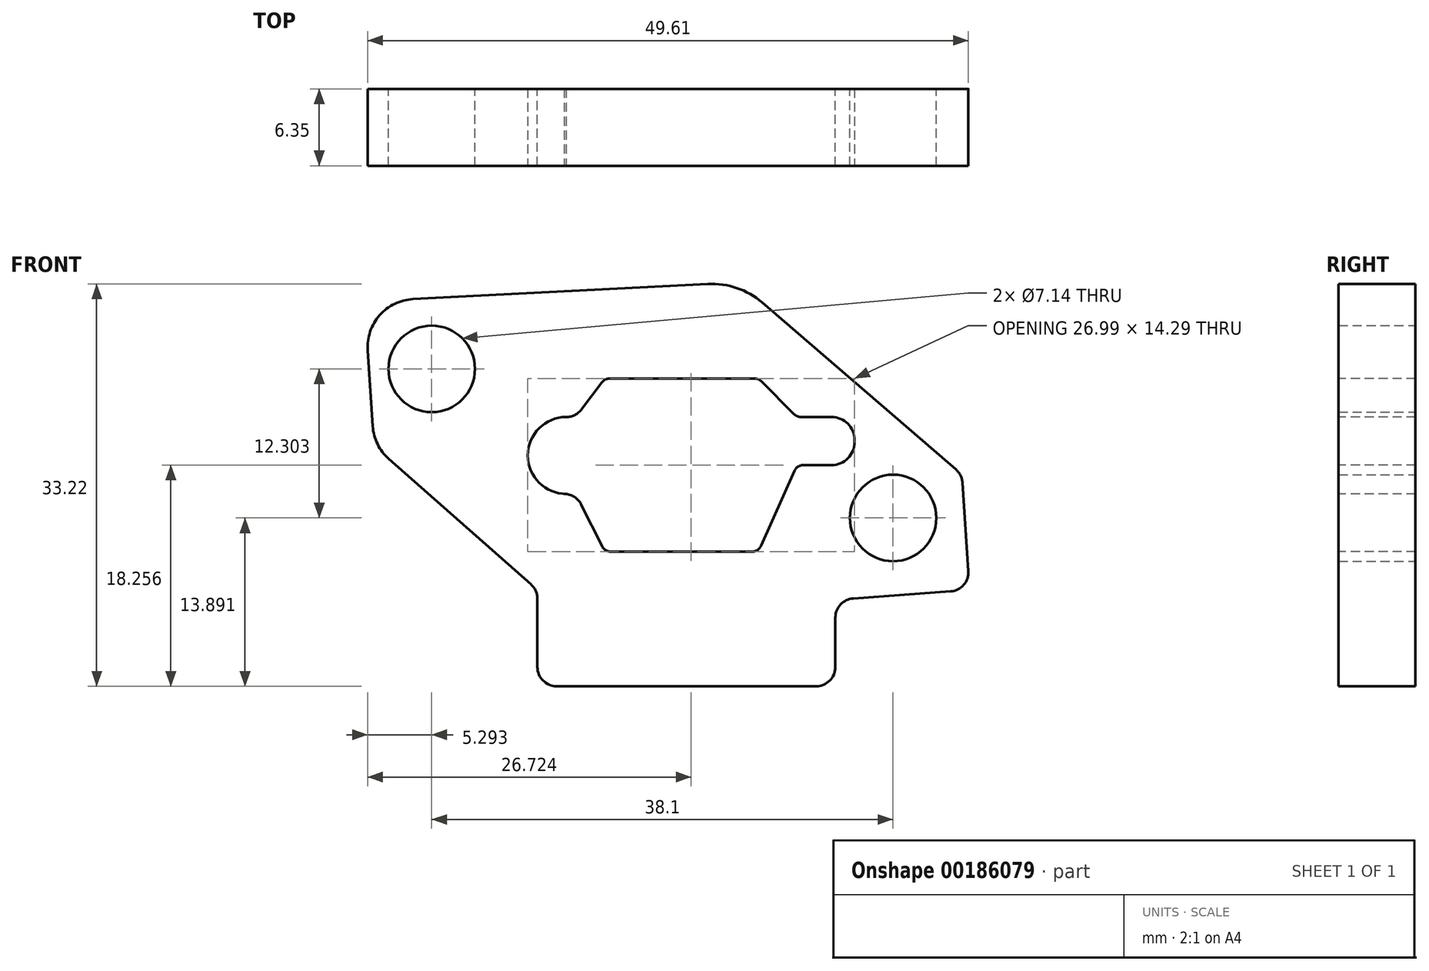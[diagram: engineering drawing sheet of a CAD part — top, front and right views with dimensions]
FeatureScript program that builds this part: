
annotation { "Feature Type Name" : "Feature", "Feature Type Description" : "" }
export const myFeature = defineFeature(function(context is Context, id is Id, definition is map)
    precondition{}
    {
        {
            var Q0;
            Q0=qCreatedBy(makeId("Front.planeOp"),FACE);
            var sketch = newSketch(context, id + "F0", { "sketchPlane" : qUnion([Q0])});
            skLineSegment(sketch, "E0", {"start": v(-1.59, 0) * mm, "end": v(-23.02, 0) * mm});
            skLineSegment(sketch, "E1", {"start": v(-24.6, 1.59) * mm, "end": v(-24.6, 7.22) * mm});
            skLineSegment(sketch, "E2", {"start": v(-25.14, 8.41) * mm, "end": v(-36.87, 18.76) * mm});
            skLineSegment(sketch, "E3", {"start": v(-38.2, 21.47) * mm, "end": v(-38.63, 27.73) * mm});
            skLineSegment(sketch, "E4", {"start": v(-34.87, 31.96) * mm, "end": v(-10.52, 33.2) * mm});
            skLineSegment(sketch, "E5", {"start": v(-6.05, 31.68) * mm, "end": v(9.95, 17.9) * mm});
            skLineSegment(sketch, "E6", {"start": v(10.5, 16.8) * mm, "end": v(10.98, 9.51) * mm});
            skLineSegment(sketch, "E7", {"start": v(9.5, 7.82) * mm, "end": v(1.47, 7.25) * mm});
            skLineSegment(sketch, "E8", {"start": v(0, 5.67) * mm, "end": v(0, 1.59) * mm});
            skPoint(sketch, "E9.visualSharp", {"position": v(-38.9, 31.75) * mm});
            skArc(sketch, "E9.filletArc", {"start": v(-34.87, 31.96) * mm, "mid": v(-37.63, 30.63) * mm, "end": v(-38.63, 27.73) * mm});
            skPoint(sketch, "E10.visualSharp", {"position": v(-38.1, 19.84) * mm});
            skArc(sketch, "E10.filletArc", {"start": v(-38.2, 21.47) * mm, "mid": v(-37.8, 19.99) * mm, "end": v(-36.87, 18.76) * mm});
            skPoint(sketch, "E11.visualSharp", {"position": v(-7.98, 33.34) * mm});
            skArc(sketch, "E11.filletArc", {"start": v(-6.05, 31.68) * mm, "mid": v(-8.14, 32.87) * mm, "end": v(-10.52, 33.2) * mm});
            skPoint(sketch, "E12.visualSharp", {"position": v(11.08, 7.94) * mm});
            skArc(sketch, "E12.filletArc", {"start": v(9.5, 7.82) * mm, "mid": v(10.6, 8.37) * mm, "end": v(10.98, 9.51) * mm});
            skPoint(sketch, "E13.visualSharp", {"position": v(10.45, 17.46) * mm});
            skArc(sketch, "E13.filletArc", {"start": v(10.5, 16.8) * mm, "mid": v(10.33, 17.4) * mm, "end": v(9.95, 17.9) * mm});
            skPoint(sketch, "E14.visualSharp", {"position": v(0, 7.14) * mm});
            skArc(sketch, "E14.filletArc", {"start": v(1.47, 7.25) * mm, "mid": v(0.43, 6.75) * mm, "end": v(0, 5.67) * mm});
            skPoint(sketch, "E15.visualSharp", {"position": v(0, 0) * mm});
            skArc(sketch, "E15.filletArc", {"start": v(-1.59, 0) * mm, "mid": v(-0.46, 0.46) * mm, "end": v(0, 1.59) * mm});
            skPoint(sketch, "E16.visualSharp", {"position": v(-24.6, 0) * mm});
            skArc(sketch, "E16.filletArc", {"start": v(-24.6, 1.59) * mm, "mid": v(-24.14, 0.46) * mm, "end": v(-23.02, 0) * mm});
            skPoint(sketch, "E17.visualSharp", {"position": v(-24.6, 7.94) * mm});
            skArc(sketch, "E17.filletArc", {"start": v(-24.6, 7.22) * mm, "mid": v(-24.75, 7.87) * mm, "end": v(-25.14, 8.41) * mm});
            skCircle(sketch, "E18", {"center": v(-33.34, 26.2) * mm, "radius": 3.57 * mm});
            skCircle(sketch, "E19", {"center": v(4.76, 13.9) * mm, "radius": 3.57 * mm});
            skSolve(sketch);
        }
        {
            var Q0;
            Q0=makeQuery(id+"F0.imprint","IMPRINT",FACE,{"disambiguationData":[TD([[makeQuery(id+"F0.imprint","IMPRINT",EDGE,{"derivedFrom":sQuery(id+"F0.wireOp",EDGE,"E0")}),-1.0]])]});
            extrude(context, id + "F1", {"entities" : qUnion([Q0]), "depth" : 6.35 * mm});
        }
        {
            var Q0;
            Q0=makeQuery(id+"F1.opExtrude","CAP_FACE",FACE,{"disambiguationData":[OSD([sQuery(id+"F0.wireOp",EDGE,"E0"),sQuery(id+"F0.wireOp",EDGE,"E1"),sQuery(id+"F0.wireOp",EDGE,"E2"),sQuery(id+"F0.wireOp",EDGE,"E3"),sQuery(id+"F0.wireOp",EDGE,"E4"),sQuery(id+"F0.wireOp",EDGE,"E5"),sQuery(id+"F0.wireOp",EDGE,"E6"),sQuery(id+"F0.wireOp",EDGE,"E7"),sQuery(id+"F0.wireOp",EDGE,"E8"),sQuery(id+"F0.wireOp",EDGE,"E9.filletArc"),sQuery(id+"F0.wireOp",EDGE,"E10.filletArc"),sQuery(id+"F0.wireOp",EDGE,"E11.filletArc"),sQuery(id+"F0.wireOp",EDGE,"E12.filletArc"),sQuery(id+"F0.wireOp",EDGE,"E13.filletArc"),sQuery(id+"F0.wireOp",EDGE,"E14.filletArc"),sQuery(id+"F0.wireOp",EDGE,"E15.filletArc"),sQuery(id+"F0.wireOp",EDGE,"E16.filletArc"),sQuery(id+"F0.wireOp",EDGE,"E17.filletArc"),sQuery(id+"F0.wireOp",EDGE,"E18"),sQuery(id+"F0.wireOp",EDGE,"E19")])],"isStart":false});
            var sketch = newSketch(context, id + "F2", { "sketchPlane" : qUnion([Q0])});
            skLineSegment(sketch, "E20", {"start": v(-18.56, 11.11) * mm, "end": v(-6.87, 11.11) * mm});
            skLineSegment(sketch, "E21", {"start": v(-6.14, 11.58) * mm, "end": v(-3.38, 17.78) * mm});
            skLineSegment(sketch, "E22", {"start": v(-2.66, 18.26) * mm, "end": v(-0.32, 18.26) * mm});
            skLineSegment(sketch, "E23", {"start": v(1.59, 20.16) * mm, "end": v(1.59, 20.32) * mm});
            skLineSegment(sketch, "E24", {"start": v(-0.32, 22.23) * mm, "end": v(-2.85, 22.23) * mm});
            skLineSegment(sketch, "E25", {"start": v(-3.4, 22.46) * mm, "end": v(-6.12, 25.17) * mm});
            skLineSegment(sketch, "E26", {"start": v(-6.68, 25.4) * mm, "end": v(-18.65, 25.4) * mm});
            skLineSegment(sketch, "E27", {"start": v(-19.29, 25.08) * mm, "end": v(-20.96, 22.86) * mm});
            skLineSegment(sketch, "E28", {"start": v(-22.23, 22.23) * mm, "end": v(-22.23, 22.23) * mm});
            skLineSegment(sketch, "E29", {"start": v(-25.4, 19.05) * mm, "end": v(-25.4, 19.05) * mm});
            skLineSegment(sketch, "E30", {"start": v(-22.41, 15.88) * mm, "end": v(-22.23, 15.88) * mm});
            skLineSegment(sketch, "E31", {"start": v(-21, 15) * mm, "end": v(-19.27, 11.55) * mm});
            skPoint(sketch, "E32.visualSharp", {"position": v(-25.4, 22.23) * mm});
            skArc(sketch, "E32.filletArc", {"start": v(-22.23, 22.23) * mm, "mid": v(-24.47, 21.3) * mm, "end": v(-25.4, 19.05) * mm});
            skPoint(sketch, "E33.visualSharp", {"position": v(-25.4, 15.88) * mm});
            skArc(sketch, "E33.filletArc", {"start": v(-25.4, 19.05) * mm, "mid": v(-24.47, 16.8) * mm, "end": v(-22.23, 15.88) * mm});
            skPoint(sketch, "E34.visualSharp", {"position": v(-21.43, 22.23) * mm});
            skArc(sketch, "E34.filletArc", {"start": v(-22.23, 22.23) * mm, "mid": v(-21.52, 22.4) * mm, "end": v(-20.96, 22.86) * mm});
            skPoint(sketch, "E35.visualSharp", {"position": v(-19.05, 25.4) * mm});
            skArc(sketch, "E35.filletArc", {"start": v(-18.65, 25.4) * mm, "mid": v(-19, 25.32) * mm, "end": v(-19.29, 25.08) * mm});
            skPoint(sketch, "E36.visualSharp", {"position": v(-6.35, 25.4) * mm});
            skArc(sketch, "E36.filletArc", {"start": v(-6.12, 25.17) * mm, "mid": v(-6.38, 25.34) * mm, "end": v(-6.68, 25.4) * mm});
            skPoint(sketch, "E37.visualSharp", {"position": v(-3.18, 22.22) * mm});
            skArc(sketch, "E37.filletArc", {"start": v(-3.4, 22.46) * mm, "mid": v(-3.15, 22.29) * mm, "end": v(-2.85, 22.23) * mm});
            skPoint(sketch, "E38.visualSharp", {"position": v(1.59, 22.23) * mm});
            skArc(sketch, "E38.filletArc", {"start": v(1.59, 20.32) * mm, "mid": v(1.03, 21.67) * mm, "end": v(-0.32, 22.23) * mm});
            skPoint(sketch, "E39.visualSharp", {"position": v(1.59, 18.26) * mm});
            skArc(sketch, "E39.filletArc", {"start": v(-0.32, 18.26) * mm, "mid": v(1.03, 18.81) * mm, "end": v(1.59, 20.16) * mm});
            skPoint(sketch, "E40.visualSharp", {"position": v(-6.35, 11.11) * mm});
            skArc(sketch, "E40.filletArc", {"start": v(-6.87, 11.11) * mm, "mid": v(-6.43, 11.24) * mm, "end": v(-6.14, 11.58) * mm});
            skPoint(sketch, "E41.visualSharp", {"position": v(-3.18, 18.26) * mm});
            skArc(sketch, "E41.filletArc", {"start": v(-2.66, 18.26) * mm, "mid": v(-3.1, 18.13) * mm, "end": v(-3.38, 17.78) * mm});
            skPoint(sketch, "E42.visualSharp", {"position": v(-19.05, 11.11) * mm});
            skArc(sketch, "E42.filletArc", {"start": v(-19.27, 11.55) * mm, "mid": v(-18.98, 11.23) * mm, "end": v(-18.56, 11.11) * mm});
            skPoint(sketch, "E43.visualSharp", {"position": v(-21.43, 15.88) * mm});
            skArc(sketch, "E43.filletArc", {"start": v(-21, 15) * mm, "mid": v(-21.58, 15.64) * mm, "end": v(-22.41, 15.88) * mm});
            skSolve(sketch);
        }
        {
            var Q0;
            Q0 = qSketchRegion(id + "F2", true);
            extrude(context, id + "F3", {"entities" : qUnion([Q0]), "operationType" : NewBodyOperationType.REMOVE, "endBound" : BoundingType.THROUGH_ALL, "oppositeDirection" : true, "depth" : 25.4 * mm});
        }
    });
